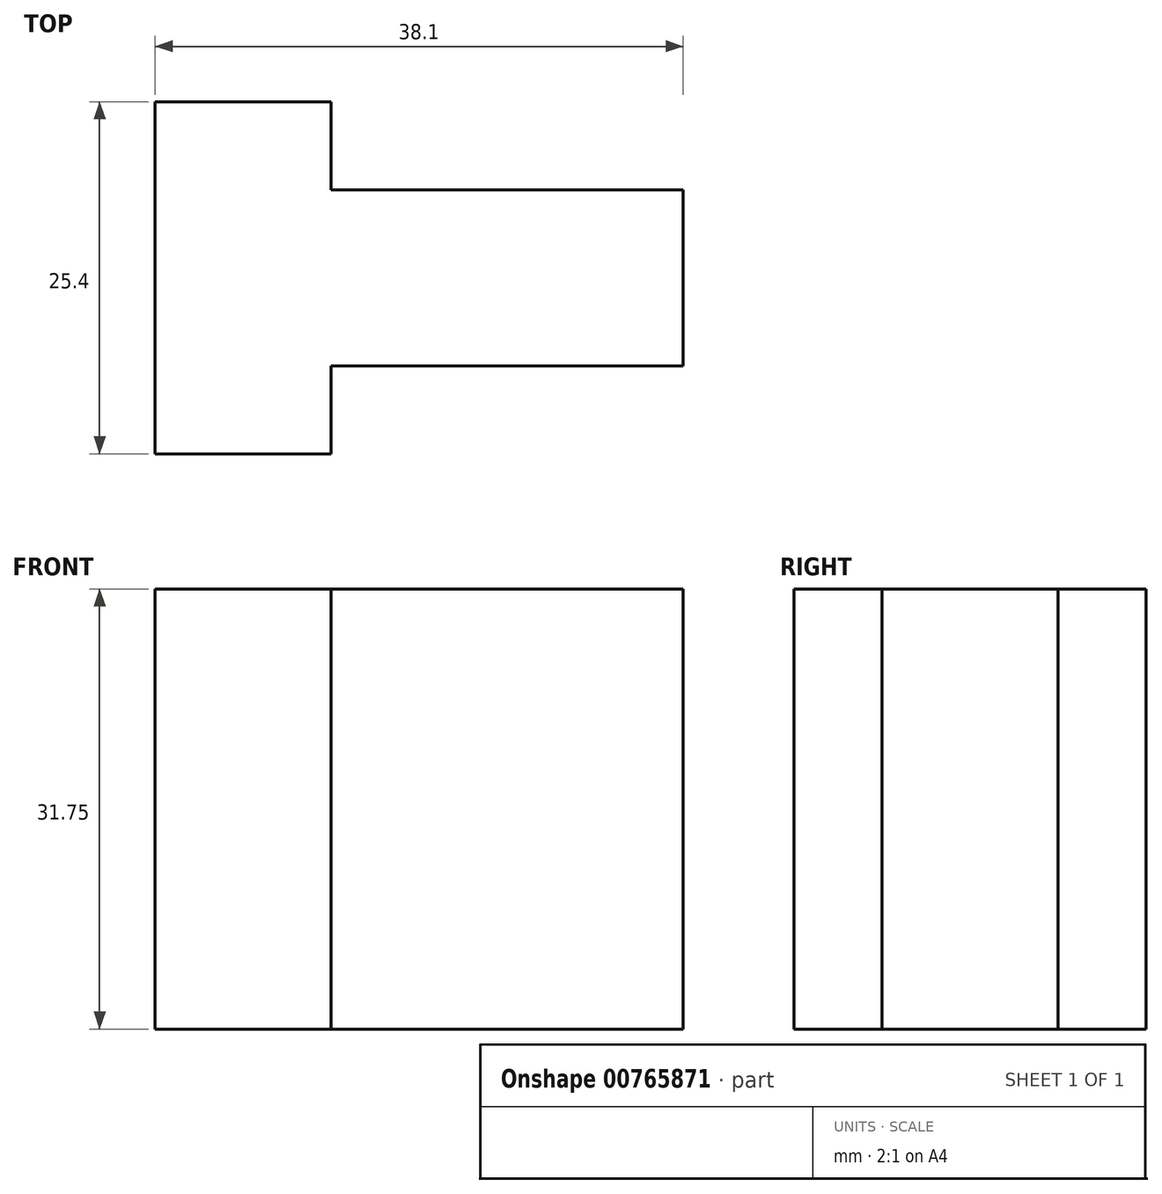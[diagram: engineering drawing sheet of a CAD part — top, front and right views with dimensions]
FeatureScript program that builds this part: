
annotation { "Feature Type Name" : "Feature", "Feature Type Description" : "" }
export const myFeature = defineFeature(function(context is Context, id is Id, definition is map)
    precondition{}
    {
        {
            var Q0;
            Q0=qCreatedBy(makeId("Top.planeOp"),FACE);
            var sketch = newSketch(context, id + "F0", { "sketchPlane" : qUnion([Q0])});
            skLineSegment(sketch, "E0", {"start": v(0, 0) * mm, "end": v(0, -6.35) * mm});
            skLineSegment(sketch, "E1", {"start": v(0, -6.35) * mm, "end": v(-12.7, -6.35) * mm});
            skLineSegment(sketch, "E2", {"start": v(0, 0) * mm, "end": v(25.4, 0) * mm});
            skLineSegment(sketch, "E3", {"start": v(25.4, 0) * mm, "end": v(25.4, 12.7) * mm});
            skLineSegment(sketch, "E4", {"start": v(25.4, 12.7) * mm, "end": v(0, 12.7) * mm});
            skLineSegment(sketch, "E5", {"start": v(0, 12.7) * mm, "end": v(0, 19.05) * mm});
            skLineSegment(sketch, "E6", {"start": v(0, 19.05) * mm, "end": v(-12.7, 19.05) * mm});
            skLineSegment(sketch, "E7", {"start": v(-12.7, 19.05) * mm, "end": v(-12.7, -6.35) * mm});
            skSolve(sketch);
        }
        {
            var Q0;
            Q0=makeQuery(id+"F0.imprint","IMPRINT",FACE,{"disambiguationData":[TD([[makeQuery(id+"F0.imprint","IMPRINT",EDGE,{"derivedFrom":sQuery(id+"F0.wireOp",EDGE,"E0")}),-1.0]])]});
            extrude(context, id + "F1", {"entities" : qUnion([Q0]), "oppositeDirection" : true, "depth" : 31.75 * mm, "offsetDistance" : 25.4 * mm});
        }
    });
